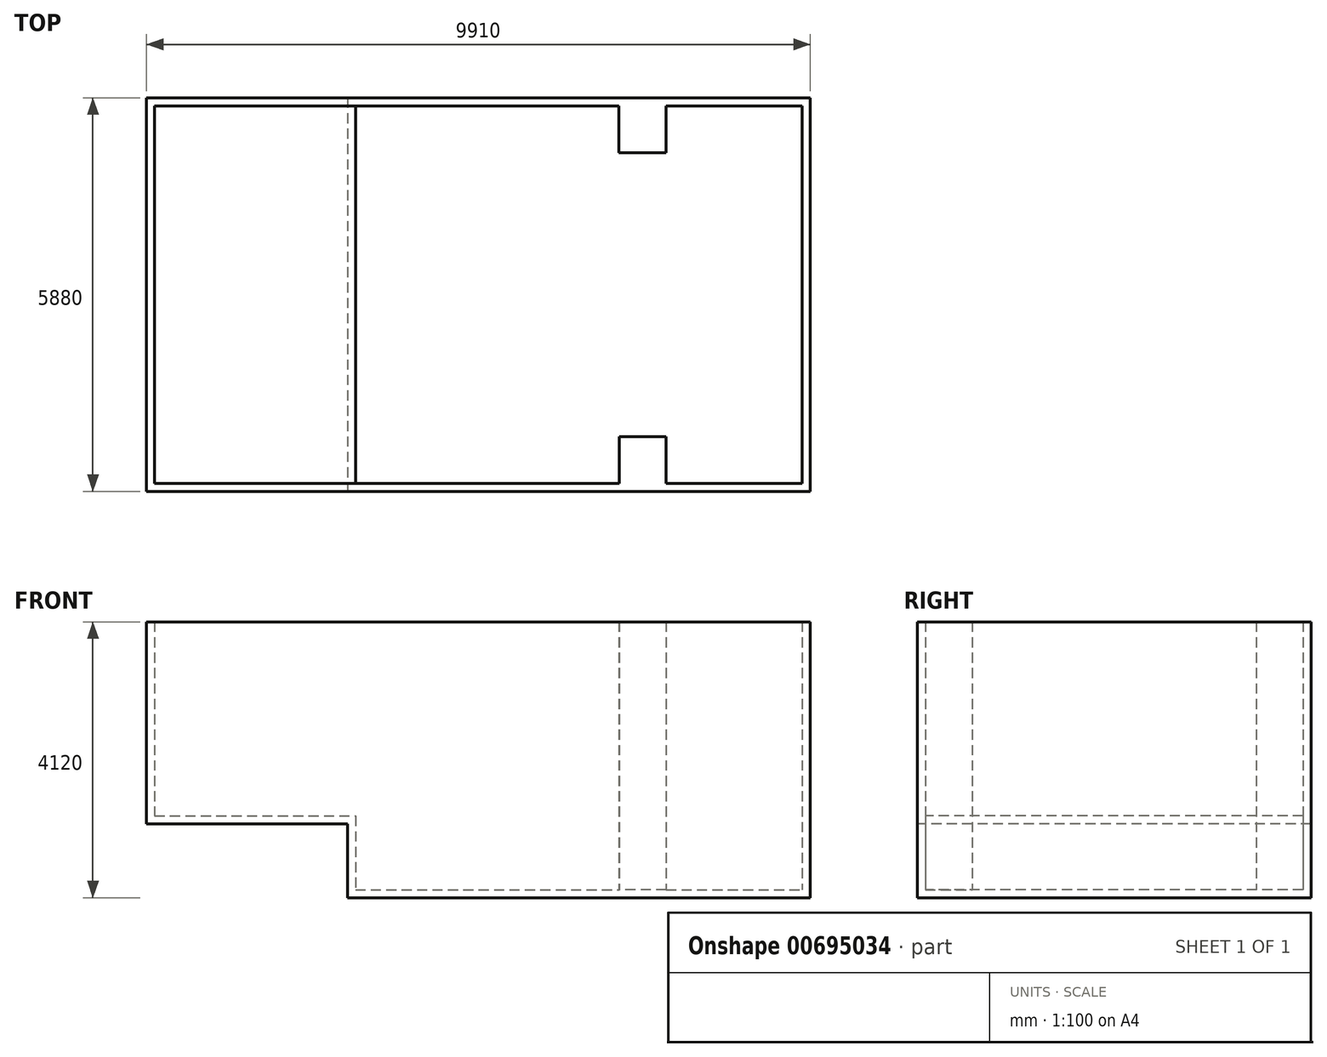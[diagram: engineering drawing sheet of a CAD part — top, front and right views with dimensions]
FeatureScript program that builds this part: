
annotation { "Feature Type Name" : "Feature", "Feature Type Description" : "" }
export const myFeature = defineFeature(function(context is Context, id is Id, definition is map)
    precondition{}
    {
        {
            var Q0;
            Q0=qCreatedBy(makeId("Top.planeOp"),FACE);
            var sketch = newSketch(context, id + "F0", { "sketchPlane" : qUnion([Q0])});
            skLineSegment(sketch, "E0.bottom", {"start": v(-3330.15, 3693.38) * mm, "end": v(3339.85, 3693.38) * mm});
            skLineSegment(sketch, "E0.top", {"start": v(-3330.15, -1946.62) * mm, "end": v(3339.85, -1946.62) * mm});
            skLineSegment(sketch, "E0.left", {"start": v(-3330.15, 3693.38) * mm, "end": v(-3330.15, -1946.62) * mm});
            skLineSegment(sketch, "E0.right", {"start": v(3339.85, 3693.38) * mm, "end": v(3339.85, -1946.62) * mm});
            skSolve(sketch);
        }
        {
            var Q0;
            Q0 = qSketchRegion(id + "F0", true);
            extrude(context, id + "F1", {"entities" : qUnion([Q0]), "depth" : 4000 * mm, "offsetDistance" : 25 * mm});
        }
        {
            var Q0;
            Q0=makeQuery(id+"F1.opExtrude","SWEPT_FACE",FACE,{"disambiguationData":[OSD([sQuery(id+"F0.wireOp",EDGE,"E0.left")])]});
            var sketch = newSketch(context, id + "F2", { "sketchPlane" : qUnion([Q0])});
            skLineSegment(sketch, "E1.bottom", {"start": v(-3693.38, 4000) * mm, "end": v(1946.62, 4000) * mm});
            skLineSegment(sketch, "E1.top", {"start": v(-3693.38, 1100) * mm, "end": v(1946.62, 1100) * mm});
            skLineSegment(sketch, "E1.left", {"start": v(-3693.38, 4000) * mm, "end": v(-3693.38, 1100) * mm});
            skLineSegment(sketch, "E1.right", {"start": v(1946.62, 4000) * mm, "end": v(1946.62, 1100) * mm});
            skSolve(sketch);
        }
        {
            var Q0;
            Q0 = qSketchRegion(id + "F2", true);
            extrude(context, id + "F3", {"entities" : qUnion([Q0]), "operationType" : NewBodyOperationType.ADD, "depth" : 3000 * mm, "offsetDistance" : 25 * mm});
        }
        {
            var Q0;
            Q0=makeQuery(id+"F3.boolean.opBoolean","MERGE",FACE,{"derivedFrom":[makeQuery(id+"F1.opExtrude","CAP_FACE",FACE,{"disambiguationData":[OSD([sQuery(id+"F0.wireOp",EDGE,"E0.bottom"),sQuery(id+"F0.wireOp",EDGE,"E0.top"),sQuery(id+"F0.wireOp",EDGE,"E0.left"),sQuery(id+"F0.wireOp",EDGE,"E0.right")])],"isStart":false}),makeQuery(id+"F3.opExtrude","SWEPT_FACE",FACE,{"disambiguationData":[OSD([sQuery(id+"F2.wireOp",EDGE,"E1.bottom")])]})]});
            shell(context, id + "F4", {"entities" : qUnion([Q0]), "thickness" : 120 * mm, "oppositeDirection" : true});
        }
        {
            var Q0;
            Q0=makeQuery(id+"F4.opShell","OFFSET_FACE",FACE,{"disambiguationData":[OSD([sQuery(id+"F0.wireOp",EDGE,"E0.bottom"),sQuery(id+"F0.wireOp",EDGE,"E0.top"),sQuery(id+"F0.wireOp",EDGE,"E0.left"),sQuery(id+"F0.wireOp",EDGE,"E0.right")])]});
            var sketch = newSketch(context, id + "F5", { "sketchPlane" : qUnion([Q0])});
            skLineSegment(sketch, "E2.bottom", {"start": v(1309.85, -1946.62) * mm, "end": v(609.85, -1946.62) * mm});
            skLineSegment(sketch, "E2.top", {"start": v(1309.85, -1246.62) * mm, "end": v(609.85, -1246.62) * mm});
            skLineSegment(sketch, "E2.left", {"start": v(1309.85, -1946.62) * mm, "end": v(1309.85, -1246.62) * mm});
            skLineSegment(sketch, "E2.right", {"start": v(609.85, -1946.62) * mm, "end": v(609.85, -1246.62) * mm});
            skLineSegment(sketch, "E3.bottom", {"start": v(1309.85, 3693.38) * mm, "end": v(599.85, 3693.38) * mm});
            skLineSegment(sketch, "E3.top", {"start": v(1309.85, 2993.38) * mm, "end": v(599.85, 2993.38) * mm});
            skLineSegment(sketch, "E3.left", {"start": v(1309.85, 3693.38) * mm, "end": v(1309.85, 2993.38) * mm});
            skLineSegment(sketch, "E3.right", {"start": v(599.85, 3693.38) * mm, "end": v(599.85, 2993.38) * mm});
            skSolve(sketch);
        }
        {
            var Q0;
            Q0 = qSketchRegion(id + "F5", true);
            var Q1;
            Q1=makeQuery(id+"F3.boolean.opBoolean","MERGE",FACE,{"derivedFrom":[makeQuery(id+"F1.opExtrude","CAP_FACE",FACE,{"disambiguationData":[OSD([sQuery(id+"F0.wireOp",EDGE,"E0.bottom"),sQuery(id+"F0.wireOp",EDGE,"E0.top"),sQuery(id+"F0.wireOp",EDGE,"E0.left"),sQuery(id+"F0.wireOp",EDGE,"E0.right")])],"isStart":false}),makeQuery(id+"F3.opExtrude","SWEPT_FACE",FACE,{"disambiguationData":[OSD([sQuery(id+"F2.wireOp",EDGE,"E1.bottom")])]})]});
            extrude(context, id + "F6", {"entities" : qUnion([Q0]), "operationType" : NewBodyOperationType.ADD, "endBound" : BoundingType.UP_TO_SURFACE, "depth" : 25 * mm, "endBoundEntityFace" : qUnion([Q1]), "offsetDistance" : 25 * mm});
        }
    });
